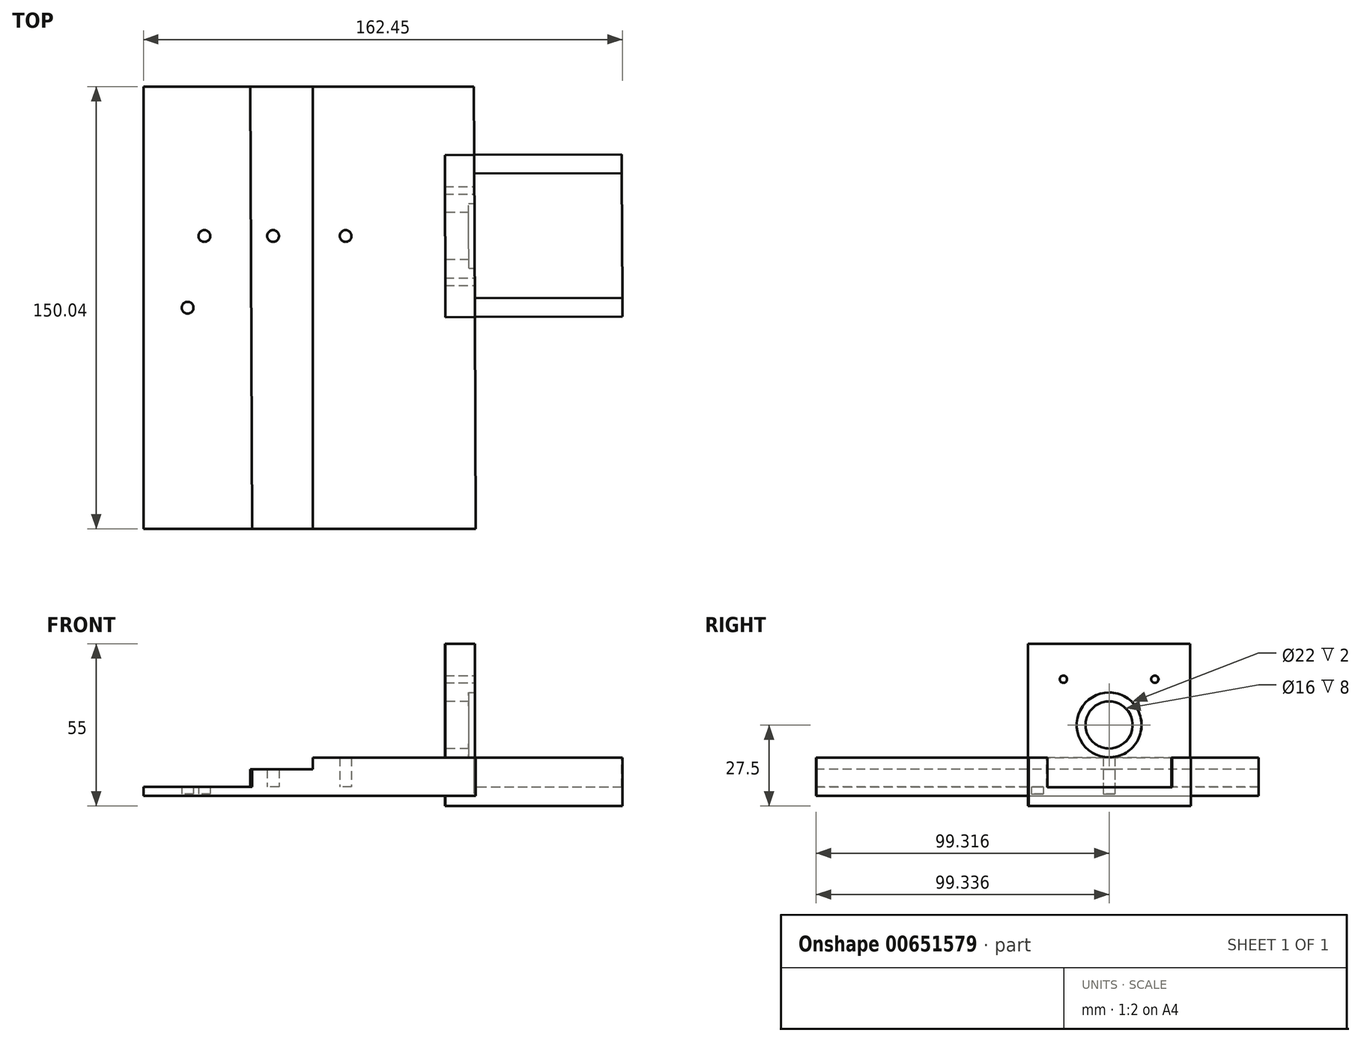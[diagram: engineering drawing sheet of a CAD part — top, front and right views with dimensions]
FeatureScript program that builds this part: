
annotation { "Feature Type Name" : "Feature", "Feature Type Description" : "" }
export const myFeature = defineFeature(function(context is Context, id is Id, definition is map)
    precondition{}
    {
        {
            var Q0;
            Q0=qCreatedBy(makeId("Top.planeOp"),FACE);
            var sketch = newSketch(context, id + "F0", { "sketchPlane" : qUnion([Q0])});
            skLineSegment(sketch, "E0.left", {"start": v(55, 51.09) * mm, "end": v(55, 11.09) * mm});
            skPoint(sketch, "E0.middle", {"position": v(0, 0) * mm});
            skLineSegment(sketch, "E1", {"start": v(-26.47, 0.43) * mm, "end": v(-3.17, 0.43) * mm});
            skCircle(sketch, "E2", {"center": v(-26.47, 0.43) * mm, "radius": 2 * mm});
            skCircle(sketch, "E3", {"center": v(-3.17, 0.43) * mm, "radius": 2 * mm});
            skCircle(sketch, "E4", {"center": v(-32.16, -23.91) * mm, "radius": 2 * mm});
            skLineSegment(sketch, "E5", {"start": v(-26.95, -98.91) * mm, "end": v(-47.16, -98.91) * mm});
            skLineSegment(sketch, "E6.bottom", {"start": v(-47.16, -98.91) * mm, "end": v(55, -98.91) * mm});
            skLineSegment(sketch, "E6.top", {"start": v(-47.16, 51.09) * mm, "end": v(55, 51.09) * mm});
            skLineSegment(sketch, "E6.left", {"start": v(-47.16, -98.91) * mm, "end": v(-47.16, 51.09) * mm});
            skLineSegment(sketch, "E6.right", {"start": v(55, -98.91) * mm, "end": v(55, 51.09) * mm});
            skLineSegment(sketch, "E7", {"start": v(-32.16, -23.91) * mm, "end": v(-47.16, -23.91) * mm});
            skSolve(sketch);
        }
        {
            var Q0;
            Q0=qSketchRegion(id+"F0",true);
            var Q1;
            Q1=makeQuery(id+"F0.imprint","IMPRINT",FACE,{"disambiguationData":[TD([[makeQuery(id+"F0.imprint","IMPRINT",EDGE,{"derivedFrom":sQuery(id+"F0.wireOp",EDGE,"E3")}),1.0]])]});
            extrude(context, id + "F1", {"entities" : qUnion([Q0, Q1]), "depth" : 3 * mm});
        }
        {
            var Q0;
            Q0=makeQuery(id+"F0.imprint","IMPRINT",FACE,{"disambiguationData":[TD([[makeQuery(id+"F0.imprint","IMPRINT",EDGE,{"derivedFrom":sQuery(id+"F0.wireOp",EDGE,"E3")}),1.0]])]});
            extrude(context, id + "F2", {"entities" : qUnion([Q0]), "operationType" : NewBodyOperationType.ADD, "depth" : 2.6 * mm});
        }
        {
            var Q0;
            Q0=makeQuery(id+"F1.opExtrude","CAP_FACE",FACE,{"disambiguationData":[OSD([sQuery(id+"F0.wireOp",EDGE,"E0.bottom"),sQuery(id+"F0.wireOp",EDGE,"E0.top"),sQuery(id+"F0.wireOp",EDGE,"E0.left"),sQuery(id+"F0.wireOp",EDGE,"E0.right"),sQuery(id+"F0.wireOp",EDGE,"lSqVqW1L-BkL0-a042-uCGb-kH9U3COpG0ft"),sQuery(id+"F0.wireOp",EDGE,"M84zw0bF-0dMt-IIN8-ISAD-6o3zNnOI7Y4u"),sQuery(id+"F0.wireOp",EDGE,"E2")])],"isStart":false});
            var sketch = newSketch(context, id + "F3", { "sketchPlane" : qUnion([Q0])});
            skLineSegment(sketch, "E8.bottom", {"start": v(-10.95, 51.09) * mm, "end": v(54.38, 51.09) * mm});
            skLineSegment(sketch, "E8.top", {"start": v(-10.33, -98.91) * mm, "end": v(55, -98.91) * mm});
            skLineSegment(sketch, "E8.right", {"start": v(54.38, 51.09) * mm, "end": v(55, -98.91) * mm});
            skLineSegment(sketch, "E9", {"start": v(-26.47, 0.43) * mm, "end": v(-3.17, 0.43) * mm});
            skPoint(sketch, "E9.endSnap0", {"position": v(-7.95, 0.43) * mm});
            skCircle(sketch, "E10", {"center": v(-3.17, 0.43) * mm, "radius": 2 * mm});
            skLineSegment(sketch, "E11", {"start": v(-3.17, 0.43) * mm, "end": v(21.43, 0.43) * mm});
            skCircle(sketch, "E12", {"center": v(21.43, 0.43) * mm, "radius": 2 * mm});
            skLineSegment(sketch, "E13", {"start": v(-10.95, 51.09) * mm, "end": v(-10.33, -98.91) * mm});
            skSolve(sketch);
        }
        {
            var Q0;
            {var subQ4=sQuery(id+"F3.wireOp",EDGE,"E8.bottom");Q0=makeQuery(id+"F3.imprint","IMPRINT",FACE,{"disambiguationData":[TD([[makeQuery(id+"F3.imprint","IMPRINT",EDGE,{"derivedFrom":subQ4}),-1.0]])]});}
            extrude(context, id + "F4", {"entities" : qUnion([Q0]), "operationType" : NewBodyOperationType.ADD, "depth" : 6 * mm});
        }
        {
            var Q0;
            Q0=makeQuery(id+"F4.opExtrude","CAP_FACE",FACE,{"disambiguationData":[OSD([sQuery(id+"F3.wireOp",EDGE,"E8.bottom"),sQuery(id+"F3.wireOp",EDGE,"E8.top"),sQuery(id+"F3.wireOp",EDGE,"E8.left"),sQuery(id+"F3.wireOp",EDGE,"E8.right"),sQuery(id+"F3.wireOp",EDGE,"E10")])],"isStart":false});
            var sketch = newSketch(context, id + "F5", { "sketchPlane" : qUnion([Q0])});
            skLineSegment(sketch, "E14", {"start": v(-3.17, 0.43) * mm, "end": v(21.43, 0.43) * mm});
            skCircle(sketch, "E15", {"center": v(21.43, 0.43) * mm, "radius": 2 * mm});
            skLineSegment(sketch, "E16.bottom", {"start": v(10.3, 51.09) * mm, "end": v(55, 51.09) * mm});
            skLineSegment(sketch, "E16.top", {"start": v(10.3, -98.91) * mm, "end": v(55, -98.91) * mm});
            skLineSegment(sketch, "E16.left", {"start": v(10.3, 51.09) * mm, "end": v(10.3, -98.91) * mm});
            skLineSegment(sketch, "E16.right", {"start": v(55, 51.09) * mm, "end": v(55, -98.91) * mm});
            skSolve(sketch);
        }
        {
            var Q0;
            Q0=makeQuery(id+"F5.imprint","IMPRINT",FACE,{"disambiguationData":[TD([[makeQuery(id+"F5.imprint","IMPRINT",EDGE,{"derivedFrom":sQuery(id+"F5.wireOp",EDGE,"E15")}),-1.0]])]});
            extrude(context, id + "F6", {"entities" : qUnion([Q0]), "operationType" : NewBodyOperationType.ADD, "depth" : 4 * mm});
        }
        {
            var Q0;
            Q0=makeQuery(id+"F0.imprint","IMPRINT",FACE,{"disambiguationData":[TD([[makeQuery(id+"F0.imprint","IMPRINT",EDGE,{"derivedFrom":sQuery(id+"F0.wireOp",EDGE,"E4")}),1.0]])]});
            var Q1;
            Q1=makeQuery(id+"F0.imprint","IMPRINT",FACE,{"disambiguationData":[TD([[makeQuery(id+"F0.imprint","IMPRINT",EDGE,{"derivedFrom":sQuery(id+"F0.wireOp",EDGE,"E2")}),1.0]])]});
            var Q2;
            Q2=qSketchRegion(id+"F3",true);
            extrude(context, id + "F7", {"entities" : qUnion([Q0, Q1, Q2]), "operationType" : NewBodyOperationType.ADD, "depth" : 0.6 * mm});
        }
        {
            var Q0;
            {var subQ0=sQuery(id+"F3.wireOp",EDGE,"E8.right");Q0=makeQuery(id+"F6.boolean.opBoolean","MERGE",FACE,{"derivedFrom":[makeQuery(id+"F4.opExtrude","SWEPT_FACE",FACE,{"disambiguationData":[OSD([subQ0])]}),makeQuery(id+"F6.opExtrude","SWEPT_FACE",FACE,{"disambiguationData":[OSD([subQ0])]})]});}
            var sketch = newSketch(context, id + "F8", { "sketchPlane" : qUnion([Q0])});
            skLineSegment(sketch, "E17.bottom", {"start": v(-99.14, 13) * mm, "end": v(50.86, 13) * mm});
            skLineSegment(sketch, "E17.top", {"start": v(-99.14, 0) * mm, "end": v(50.86, 0) * mm});
            skLineSegment(sketch, "E17.left", {"start": v(-99.14, 13) * mm, "end": v(-99.14, 0) * mm});
            skLineSegment(sketch, "E17.right", {"start": v(50.86, 13) * mm, "end": v(50.86, 0) * mm});
            skSolve(sketch);
        }
        {
            var Q0;
            Q0=qSketchRegion(id+"F8",true);
            extrude(context, id + "F9", {"entities" : qUnion([Q0]), "operationType" : NewBodyOperationType.ADD, "depth" : 10.6 * mm});
        }
        {
            var Q0;
            Q0=makeQuery(id+"F9.opExtrude","CAP_FACE",FACE,{"disambiguationData":[OSD([sQuery(id+"F8.wireOp",EDGE,"E17.bottom"),sQuery(id+"F8.wireOp",EDGE,"E17.top"),sQuery(id+"F8.wireOp",EDGE,"E17.left"),sQuery(id+"F8.wireOp",EDGE,"E17.right")])],"isStart":false});
            var sketch = newSketch(context, id + "F10", { "sketchPlane" : qUnion([Q0])});
            skLineSegment(sketch, "E18", {"start": v(0.16, 13) * mm, "end": v(0.16, 24.05) * mm});
            skLineSegment(sketch, "E19", {"start": v(-0.27, 9.43) * mm, "end": v(0.16, 9.43) * mm});
            skLineSegment(sketch, "E20.bottom", {"start": v(15.66, 39.55) * mm, "end": v(-15.34, 39.55) * mm});
            skLineSegment(sketch, "E20.top", {"start": v(15.66, 8.55) * mm, "end": v(-15.34, 8.55) * mm});
            skLineSegment(sketch, "E20.left", {"start": v(15.66, 39.55) * mm, "end": v(15.66, 8.55) * mm});
            skLineSegment(sketch, "E20.right", {"start": v(-15.34, 39.55) * mm, "end": v(-15.34, 8.55) * mm});
            skPoint(sketch, "E20.middle", {"position": v(0.16, 24.05) * mm});
            skLineSegment(sketch, "E21.bottom", {"start": v(-20.99, 45.2) * mm, "end": v(21.31, 45.2) * mm});
            skLineSegment(sketch, "E21.top", {"start": v(-20.99, 2.9) * mm, "end": v(21.31, 2.9) * mm});
            skLineSegment(sketch, "E21.left", {"start": v(-20.99, 45.2) * mm, "end": v(-20.99, 2.9) * mm});
            skLineSegment(sketch, "E21.right", {"start": v(21.31, 45.2) * mm, "end": v(21.31, 2.9) * mm});
            skLineSegment(sketch, "E22.bottom", {"start": v(-27.34, 51.55) * mm, "end": v(27.66, 51.55) * mm});
            skLineSegment(sketch, "E22.top", {"start": v(-27.34, -3.45) * mm, "end": v(27.66, -3.45) * mm});
            skLineSegment(sketch, "E22.left", {"start": v(-27.34, 51.55) * mm, "end": v(-27.34, -3.45) * mm});
            skLineSegment(sketch, "E22.right", {"start": v(27.66, 51.55) * mm, "end": v(27.66, -3.45) * mm});
            skCircle(sketch, "E23", {"center": v(0.16, 24.05) * mm, "radius": 11 * mm});
            skCircle(sketch, "E24", {"center": v(-15.34, 39.55) * mm, "radius": 1.25 * mm});
            skCircle(sketch, "E25", {"center": v(15.66, 39.55) * mm, "radius": 1.25 * mm});
            skCircle(sketch, "E26", {"center": v(-15.34, 8.55) * mm, "radius": 1.25 * mm});
            skCircle(sketch, "E27", {"center": v(15.66, 8.55) * mm, "radius": 1.25 * mm});
            skSolve(sketch);
        }
        {
            var Q0;
            Q0=makeQuery(id+"F10.imprint","IMPRINT",FACE,{"disambiguationData":[TD([[makeQuery(id+"F10.imprint","IMPRINT",EDGE,{"derivedFrom":sQuery(id+"F10.wireOp",EDGE,"E23")}),-1.0]])]});
            var Q1;
            {var subQ0=sQuery(id+"F10.wireOp",EDGE,"E21.bottom");Q1=makeQuery(id+"F10.imprint","IMPRINT",FACE,{"disambiguationData":[TD([[makeQuery(id+"F10.imprint","IMPRINT",EDGE,{"derivedFrom":subQ0}),-1.0]])]});}
            var Q2;
            {var subQ2=sQuery(id+"F10.wireOp",EDGE,"E21.bottom");Q2=makeQuery(id+"F10.imprint","IMPRINT",FACE,{"disambiguationData":[TD([[makeQuery(id+"F10.imprint","IMPRINT",EDGE,{"derivedFrom":subQ2}),1.0]])]});}
            var Q3;
            {var subQ0=sQuery(id+"F10.wireOp",EDGE,"E22.top");Q3=makeQuery(id+"F10.imprint","IMPRINT",FACE,{"disambiguationData":[TD([[makeQuery(id+"F10.imprint","IMPRINT",EDGE,{"derivedFrom":subQ0}),1.0]])]});}
            extrude(context, id + "F11", {"entities" : qUnion([Q0, Q1, Q2, Q3]), "operationType" : NewBodyOperationType.ADD, "oppositeDirection" : true, "depth" : 10 * mm});
        }
        {
            var Q0;
            Q0=makeQuery(id+"F11.opExtrude","CAP_FACE",FACE,{"disambiguationData":[OSD([sQuery(id+"F8.wireOp",EDGE,"E17.bottom"),sQuery(id+"F10.wireOp",EDGE,"E22.bottom"),sQuery(id+"F10.wireOp",EDGE,"E22.left"),sQuery(id+"F10.wireOp",EDGE,"E22.right"),sQuery(id+"F10.wireOp",EDGE,"E23"),sQuery(id+"F10.wireOp",EDGE,"E24"),sQuery(id+"F10.wireOp",EDGE,"E25")])],"isStart":false});
            var sketch = newSketch(context, id + "F12", { "sketchPlane" : qUnion([Q0])});
            skCircle(sketch, "E28", {"center": v(-0.16, 24.05) * mm, "radius": 11 * mm});
            skCircle(sketch, "E29", {"center": v(-0.16, 24.05) * mm, "radius": 8 * mm});
            skSolve(sketch);
        }
        {
            var Q0;
            Q0=makeQuery(id+"F12.imprint","IMPRINT",FACE,{"disambiguationData":[TD([[makeQuery(id+"F12.imprint","IMPRINT",EDGE,{"derivedFrom":sQuery(id+"F12.wireOp",EDGE,"E28")}),-1.0]])]});
            extrude(context, id + "F13", {"entities" : qUnion([Q0]), "operationType" : NewBodyOperationType.ADD, "oppositeDirection" : true, "depth" : 8 * mm});
        }
        {
            var Q0;
            {var subQ0=sQuery(id+"F10.wireOp",EDGE,"E22.right");var subQ1=sQuery(id+"F10.wireOp",EDGE,"E22.left");var subQ2=sQuery(id+"F8.wireOp",EDGE,"E17.top");var subQ3=sQuery(id+"F8.wireOp",EDGE,"E17.bottom");Q0=makeQuery(id+"F11.boolean.opBoolean","MERGE",FACE,{"derivedFrom":[makeQuery(id+"F9.opExtrude","CAP_FACE",FACE,{"disambiguationData":[OSD([subQ3,subQ2,sQuery(id+"F8.wireOp",EDGE,"E17.left"),sQuery(id+"F8.wireOp",EDGE,"E17.right")])],"isStart":false}),makeQuery(id+"F11.opExtrude","CAP_FACE",FACE,{"disambiguationData":[OSD([subQ3,sQuery(id+"F10.wireOp",EDGE,"E22.bottom"),subQ1,subQ0,sQuery(id+"F10.wireOp",EDGE,"E23"),sQuery(id+"F10.wireOp",EDGE,"E24"),sQuery(id+"F10.wireOp",EDGE,"E25")])],"isStart":true}),makeQuery(id+"F11.opExtrude","CAP_FACE",FACE,{"disambiguationData":[OSD([subQ2,sQuery(id+"F10.wireOp",EDGE,"E22.top"),subQ1,subQ0])],"isStart":true})]});}
            var sketch = newSketch(context, id + "F14", { "sketchPlane" : qUnion([Q0])});
            skLineSegment(sketch, "E30.bottom", {"start": v(-27.34, -3.45) * mm, "end": v(27.66, -3.45) * mm});
            skLineSegment(sketch, "E30.top", {"start": v(-20.99, 2.9) * mm, "end": v(21.31, 2.9) * mm});
            skLineSegment(sketch, "E30.left", {"start": v(-27.34, -3.45) * mm, "end": v(-27.34, 2.9) * mm});
            skLineSegment(sketch, "E30.right", {"start": v(27.66, -3.45) * mm, "end": v(27.66, 2.9) * mm});
            skLineSegment(sketch, "E31.top", {"start": v(-27.34, 12.9) * mm, "end": v(-20.99, 12.9) * mm});
            skLineSegment(sketch, "E31.left", {"start": v(-27.34, 2.9) * mm, "end": v(-27.34, 12.9) * mm});
            skLineSegment(sketch, "E31.right", {"start": v(-20.99, 2.9) * mm, "end": v(-20.99, 12.9) * mm});
            skLineSegment(sketch, "E32.top", {"start": v(27.66, 12.9) * mm, "end": v(21.31, 12.9) * mm});
            skLineSegment(sketch, "E32.left", {"start": v(27.66, 2.9) * mm, "end": v(27.66, 12.9) * mm});
            skLineSegment(sketch, "E32.right", {"start": v(21.31, 2.9) * mm, "end": v(21.31, 12.9) * mm});
            skSolve(sketch);
        }
        {
            var Q0;
            {var subQ23=sQuery(id+"F14.wireOp",EDGE,"E30.bottom");Q0=makeQuery(id+"F14.imprint","IMPRINT",FACE,{"disambiguationData":[TD([[makeQuery(id+"F14.imprint","IMPRINT",EDGE,{"derivedFrom":subQ23}),1.0]])]});}
            extrude(context, id + "F15", {"entities" : qUnion([Q0]), "operationType" : NewBodyOperationType.ADD, "depth" : 50 * mm});
        }
    });
